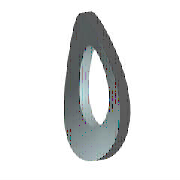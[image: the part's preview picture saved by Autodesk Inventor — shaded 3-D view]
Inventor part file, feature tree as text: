
AUTODESK INVENTOR PART (.ipt)
format: ipt  version: 2022 (Build 260153000, 153)  size: 108,032 bytes
history: native  units: mm (DEFAULTED — no unit token found)
features: other x1, plane x1, sketch x1
ambient origin geometry x7: Origin, YZ Plane, XY Plane, X Axis, Y Axis, Z Axis, Center Point
bodies: Solid1 (feature_tree), Body (feature_tree)
feature tree (3):
  other  "Work Axis1"
  plane  "Work Plane1"
  sketch  "Sketch"  dims[d0=10.5mm d1=21.0mm d2=1.0mm d3=0.0mm d4=0.0mm d5=0.0mm d6=0.0mm d7=0.0mm]
